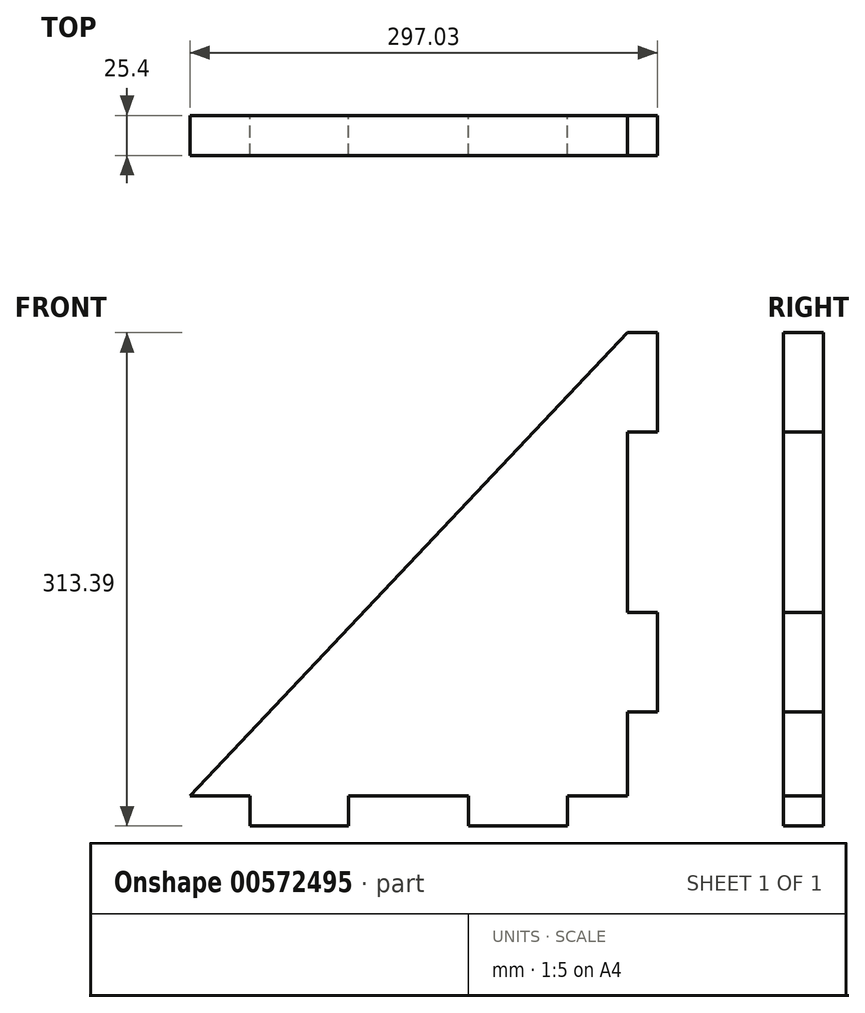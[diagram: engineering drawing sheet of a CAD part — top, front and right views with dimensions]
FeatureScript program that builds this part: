
annotation { "Feature Type Name" : "Feature", "Feature Type Description" : "" }
export const myFeature = defineFeature(function(context is Context, id is Id, definition is map)
    precondition{}
    {
        {
            var Q0;
            Q0=qCreatedBy(makeId("Front.planeOp"),FACE);
            var sketch = newSketch(context, id + "F0", { "sketchPlane" : qUnion([Q0])});
            skLineSegment(sketch, "E0", {"start": v(-52.62, 10.4) * mm, "end": v(-14.52, 10.4) * mm});
            skLineSegment(sketch, "E1", {"start": v(-14.52, 10.4) * mm, "end": v(-14.52, -8.72) * mm});
            skLineSegment(sketch, "E2", {"start": v(-14.52, -8.72) * mm, "end": v(48.22, -8.72) * mm});
            skLineSegment(sketch, "E3", {"start": v(48.22, -8.72) * mm, "end": v(48.22, 10.4) * mm});
            skLineSegment(sketch, "E4", {"start": v(48.22, 10.4) * mm, "end": v(124.45, 10.4) * mm});
            skLineSegment(sketch, "E5", {"start": v(124.45, 10.4) * mm, "end": v(124.45, -8.72) * mm});
            skLineSegment(sketch, "E6", {"start": v(124.45, -8.72) * mm, "end": v(187.19, -8.72) * mm});
            skLineSegment(sketch, "E7", {"start": v(187.19, -8.72) * mm, "end": v(187.19, 10.4) * mm});
            skLineSegment(sketch, "E8", {"start": v(187.19, 10.4) * mm, "end": v(225.29, 10.4) * mm});
            skLineSegment(sketch, "E9", {"start": v(225.29, 10.4) * mm, "end": v(225.29, 63.75) * mm});
            skLineSegment(sketch, "E10", {"start": v(225.29, 63.75) * mm, "end": v(244.41, 63.75) * mm});
            skLineSegment(sketch, "E11", {"start": v(244.41, 63.75) * mm, "end": v(244.41, 127) * mm});
            skLineSegment(sketch, "E12", {"start": v(244.41, 127) * mm, "end": v(225.29, 127) * mm});
            skLineSegment(sketch, "E13", {"start": v(225.29, 127) * mm, "end": v(225.29, 241.42) * mm});
            skLineSegment(sketch, "E14", {"start": v(225.29, 241.42) * mm, "end": v(244.41, 241.42) * mm});
            skLineSegment(sketch, "E15", {"start": v(244.41, 241.42) * mm, "end": v(244.41, 304.67) * mm});
            skLineSegment(sketch, "E16", {"start": v(244.41, 304.67) * mm, "end": v(225.29, 304.67) * mm});
            skLineSegment(sketch, "E17", {"start": v(225.29, 304.67) * mm, "end": v(-52.62, 10.4) * mm});
            skSolve(sketch);
        }
        {
            var Q0;
            Q0 = qSketchRegion(id + "F0", true);
            extrude(context, id + "F1", {"entities" : qUnion([Q0]), "depth" : 25.4 * mm, "offsetDistance" : 25.4 * mm});
        }
    });
